# Revit family: floodlight_fl_21_iq_midi___pl61_5xa7781f4c1a_146e
name_source: partatom
category: Lighting Fixtures
units: mm (PartAtom-declared; Revit-internal decimal feet)

## family parameters
Cut with Voids When Loaded = No
Host = Face
Light Source = No
Part Type = Normal
Room Calculation Point = No
Round Connector Dimension = Use Diameter
Shared = No

## types (1)
- --- (1 x LED, 36650 lm, 270.2 W, 4000K)
    Apparent Load = 270 VA
    CIE Flux Codes = 33 65 98 100 100
    Color Rendering = 70
    Color Temperature = 4000K
    Default Elevation = 1800 mm
    Description = Floodlight FL 21 iQ midi, floodlight, primary light control with lens, of PMMA, primary optical cover: protective disc, of toughened safety glass, transparent, light distribution: PL61, light emission: direct distribution, installation type: surface-mounted, lamps: LED, High Power LED, rated values: 36.650lm | 270,2W | 135,6lm/W (begin service life); end service life: 36.650lm | 286,6W; at 50% lumin. flux: 18.325lm | 117,7W | 155,7lm/W, colour temperature: 4000K, colour rendering: CRI > 70, light colour: 740, light setting 1 begin service life: 100% | 36.650lm | 270,2W | 135,6lm/W | 4.000K, light setting 1 end service life: 286,6W, further light settings possible, control: optimised constant luminous flux control (CLO 2.0), Desk-Remote (wireless, voltage-free reading and setting of iQ features in the workshop via application-optimized NFC function/RFID function), Light-Fading, Smart-Wire, Night-Set, Lumen-Switch, Temp-Guard, Auto-Match, pre-setting: linear dimming characteristic, with terminal, 6-pole, mains connection: 220..240V, AC, 50/60Hz, luminaire housing, of diecast aluminium, powder-coated, SITECO metallic grey (DB 702S), corrosivity category C5 mid according to DIN EN ISO 12944suitable for swimming poolschlorine-resistant, sealing non-destructively replaceable, mounting bracket, of steel, galvanised, powder-coated, SITECO metallic grey (DB 702S), protection rating (complete): IP66, insulation class (complete): insulation class II (safety insulation), certification: CE, ENEC, VDE, protection symbol: D, impact resistance: IK08, permissible operating ambient temperature: -40..+40°C, permissible operating ambient temperature for outdoor applications: -40..+50°C, standard: DIN EN 12944, LABS conformity tested according to VDMA 24364:2018-05, packaging unit: 1 piece

Light Distribution: PL61
    Height = 76 mm
    Lamp = 1 x LED
    Lamp Light Flux = 36650 lm
    Lamp Power = 270.2 W
    Lamp count = 1
    Length = 657 mm
    Luminous efficacy = 136 lm/W
    Manufacturer = Siteco
    ModVariant = No
    Model = 5XA7781F4C1A
    Mounting Place = Pole
    Mounting Type = Pole annexe
    Number of Poles = 1
    OnlyDefault = Yes
    Power Factor = 1
    Product Name = Floodlight FL 21 iQ midi | PL61
    Product group = floodlight | pylon annexe
    ProductGroupID = 6201
    Protection Class = Protection class II
    Protection Degree = IP 66
    RLX_Detail_Level = 1
    RLX_Emergency_Light_Flux = 0 lm
    RLX_Emergency_Type = 0
    RLX_Emergency_Type_DB = No
    RlxData = <blob elided: 147141 chars, md5=b7a4cf03>
    Socket = socket
    Standby Power = 0 W
    System Light Flux = 36650 lm
    System Power = 270 W
    Type Comments = factory setting: luminous flux: 100 % | dim-lin: 254 | 620 mA
    Type Image = l_1006876.jpg
    URL = http://relux.com
    VarID = @adj_109951
    Voltage = 0 V
    Weight = 0.00 kg
    Width = 442 mm

## geometry (parser evidence)
native form markers: Sweep x15
no freeform markers — native parametric forms only
